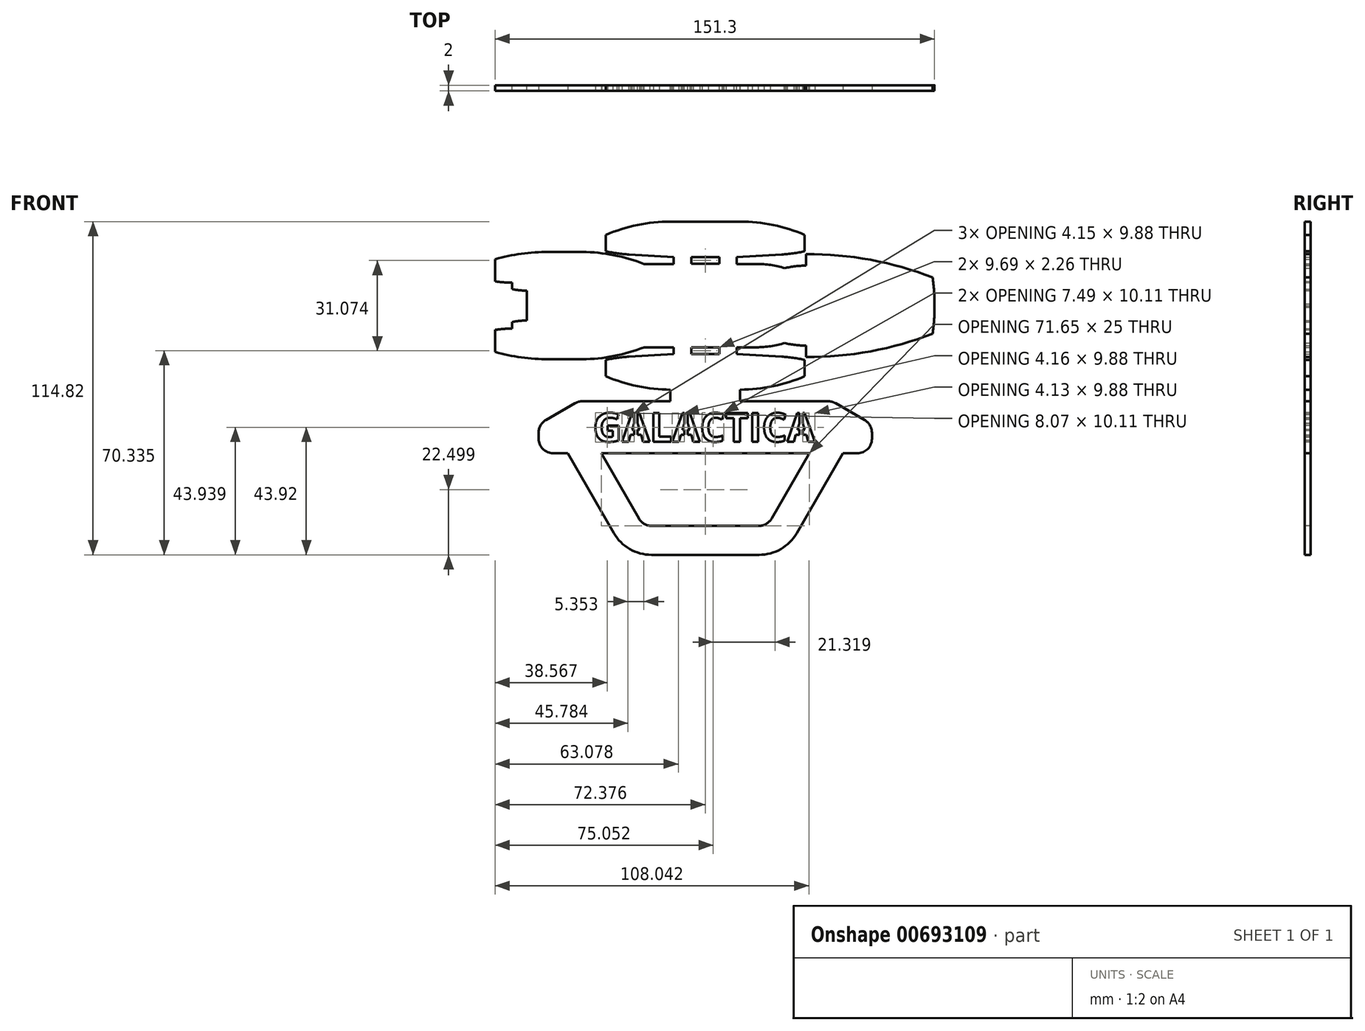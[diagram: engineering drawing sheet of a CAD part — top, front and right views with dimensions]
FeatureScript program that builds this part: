
annotation { "Feature Type Name" : "Feature", "Feature Type Description" : "" }
export const myFeature = defineFeature(function(context is Context, id is Id, definition is map)
    precondition{}
    {
        {
            var Q0;
            Q0=qCreatedBy(makeId("Front.planeOp"),FACE);
            var sketch = newSketch(context, id + "F0", { "sketchPlane" : qUnion([Q0])});
            skLineSegment(sketch, "E0", {"start": v(0, 27.3) * mm, "end": v(0, 0) * mm, "construction": true});
            skLineSegment(sketch, "E1", {"start": v(0, 0) * mm, "end": v(-65, 0) * mm, "construction": true});
            skArc(sketch, "E2", {"start": v(-25.69, 14.25) * mm, "mid": v(-44.18, 12.64) * mm, "end": v(-62.02, 7.56) * mm});
            skArc(sketch, "E3", {"start": v(-62.02, 7.56) * mm, "mid": v(-62.42, 3.79) * mm, "end": v(-62.55, 0) * mm});
            skLineSegment(sketch, "E4", {"start": v(-25.69, 14.25) * mm, "end": v(-25.69, 10.95) * mm});
            skArc(sketch, "E5", {"start": v(-19.6, 10.24) * mm, "mid": v(-22.62, 10.8) * mm, "end": v(-25.69, 10.95) * mm});
            skArc(sketch, "E6", {"start": v(-11.48, 11.46) * mm, "mid": v(-15.58, 11.15) * mm, "end": v(-19.6, 10.24) * mm});
            skLineSegment(sketch, "E7", {"start": v(-11.48, 11.46) * mm, "end": v(-5.84, 11.46) * mm});
            skLineSegment(sketch, "E8", {"start": v(-5.84, 11.46) * mm, "end": v(-5.84, 13.41) * mm});
            skLineSegment(sketch, "E9", {"start": v(-0.82, 11.5) * mm, "end": v(-0.82, 13.39) * mm});
            skLineSegment(sketch, "E10", {"start": v(-25.28, 19.79) * mm, "end": v(-25.28, 15.07) * mm});
            skArc(sketch, "E11", {"start": v(-25.28, 15.07) * mm, "mid": v(-22, 14.5) * mm, "end": v(-18.68, 14.17) * mm});
            skLineSegment(sketch, "E12", {"start": v(-18.68, 14.17) * mm, "end": v(-5.84, 13.41) * mm});
            skLineSegment(sketch, "E13", {"start": v(3.22, 14.5) * mm, "end": v(3.22, 0) * mm, "construction": true});
            skLineSegment(sketch, "E14.MirrorCS", {"start": v(7.26, 11.5) * mm, "end": v(7.26, 13.39) * mm});
            skLineSegment(sketch, "E15.MirrorCS", {"start": v(12.28, 11.46) * mm, "end": v(12.28, 13.41) * mm});
            skLineSegment(sketch, "E16.MirrorCS", {"start": v(31.72, 19.79) * mm, "end": v(31.72, 15.07) * mm});
            skLineSegment(sketch, "E17.MirrorCS", {"start": v(25.12, 14.17) * mm, "end": v(12.28, 13.41) * mm});
            skArc(sketch, "E18.MirrorCS", {"start": v(31.72, 15.07) * mm, "mid": v(28.44, 14.5) * mm, "end": v(25.12, 14.17) * mm});
            skArc(sketch, "E19", {"start": v(-6.78, 23.62) * mm, "mid": v(-16.23, 22.66) * mm, "end": v(-25.28, 19.79) * mm});
            skLineSegment(sketch, "E20", {"start": v(-6.78, 23.62) * mm, "end": v(13.22, 23.62) * mm});
            skArc(sketch, "E21.MirrorCS", {"start": v(13.22, 23.62) * mm, "mid": v(22.67, 22.66) * mm, "end": v(31.72, 19.79) * mm});
            skLineSegment(sketch, "E22", {"start": v(-0.82, 11.5) * mm, "end": v(7.26, 11.5) * mm});
            skLineSegment(sketch, "E23", {"start": v(-0.82, 13.39) * mm, "end": v(7.26, 13.39) * mm});
            skLineSegment(sketch, "E24", {"start": v(12.28, 11.46) * mm, "end": v(20.77, 11.46) * mm});
            skArc(sketch, "E25", {"start": v(38.48, 14.9) * mm, "mid": v(29.46, 14) * mm, "end": v(20.77, 11.46) * mm});
            skLineSegment(sketch, "E26", {"start": v(38.48, 14.9) * mm, "end": v(48.28, 14.9) * mm});
            skArc(sketch, "E27", {"start": v(63.53, 12.8) * mm, "mid": v(55.98, 14.37) * mm, "end": v(48.28, 14.9) * mm});
            skLineSegment(sketch, "E28", {"start": v(63.53, 12.8) * mm, "end": v(63.53, 6.47) * mm});
            skArc(sketch, "E29", {"start": v(58.7, 6.1) * mm, "mid": v(61.12, 6.19) * mm, "end": v(63.53, 6.47) * mm});
            skLineSegment(sketch, "E30", {"start": v(58.7, 6.1) * mm, "end": v(58.7, 4.24) * mm});
            skArc(sketch, "E31", {"start": v(54.38, 3.77) * mm, "mid": v(56.55, 3.9) * mm, "end": v(58.7, 4.24) * mm});
            skLineSegment(sketch, "E32", {"start": v(54.38, 3.77) * mm, "end": v(54.38, 0) * mm});
            skLineSegment(sketch, "E33", {"start": v(-62.55, 0) * mm, "end": v(-62.55, -0.5) * mm});
            skLineSegment(sketch, "E34", {"start": v(-62.55, -0.5) * mm, "end": v(54.38, -0.5) * mm, "construction": true});
            skLineSegment(sketch, "E35", {"start": v(54.38, -0.5) * mm, "end": v(54.38, 0) * mm});
            skArc(sketch, "E36.MirrorCS", {"start": v(58.7, -7.1) * mm, "mid": v(61.12, -7.19) * mm, "end": v(63.53, -7.47) * mm});
            skLineSegment(sketch, "E37.MirrorCS", {"start": v(-0.82, -12.5) * mm, "end": v(-0.82, -14.39) * mm});
            skLineSegment(sketch, "E38.MirrorCS", {"start": v(-25.28, -20.79) * mm, "end": v(-25.28, -16.07) * mm});
            skArc(sketch, "E39.MirrorCS", {"start": v(-25.28, -16.07) * mm, "mid": v(-22, -15.5) * mm, "end": v(-18.68, -15.17) * mm});
            skLineSegment(sketch, "E40.MirrorCS", {"start": v(58.7, -7.1) * mm, "end": v(58.7, -5.24) * mm});
            skLineSegment(sketch, "E41.MirrorCS", {"start": v(7.26, -12.5) * mm, "end": v(7.26, -14.39) * mm});
            skLineSegment(sketch, "E42.MirrorCS", {"start": v(54.38, -4.77) * mm, "end": v(54.38, -1) * mm});
            skLineSegment(sketch, "E43.MirrorCS", {"start": v(12.28, -12.46) * mm, "end": v(12.28, -14.41) * mm});
            skLineSegment(sketch, "E44.MirrorCS", {"start": v(-62.55, -1) * mm, "end": v(-62.55, -0.5) * mm});
            skArc(sketch, "E45.MirrorCS", {"start": v(54.38, -4.77) * mm, "mid": v(56.55, -4.9) * mm, "end": v(58.7, -5.24) * mm});
            skLineSegment(sketch, "E46.MirrorCS", {"start": v(-25.69, -15.25) * mm, "end": v(-25.69, -11.95) * mm});
            skLineSegment(sketch, "E47.MirrorCS", {"start": v(31.72, -20.79) * mm, "end": v(31.72, -16.07) * mm});
            skLineSegment(sketch, "E48.MirrorCS", {"start": v(54.38, -0.5) * mm, "end": v(54.38, -1) * mm});
            skLineSegment(sketch, "E49.MirrorCS", {"start": v(-5.84, -12.46) * mm, "end": v(-5.84, -14.41) * mm});
            skLineSegment(sketch, "E50.MirrorCS", {"start": v(-11.48, -12.46) * mm, "end": v(-5.84, -12.46) * mm});
            skArc(sketch, "E51.MirrorCS", {"start": v(-19.6, -11.24) * mm, "mid": v(-22.62, -11.8) * mm, "end": v(-25.69, -11.95) * mm});
            skLineSegment(sketch, "E52.MirrorCS", {"start": v(-0.82, -12.5) * mm, "end": v(7.26, -12.5) * mm});
            skLineSegment(sketch, "E53.MirrorCS", {"start": v(-0.82, -14.39) * mm, "end": v(7.26, -14.39) * mm});
            skArc(sketch, "E54.MirrorCS", {"start": v(13.22, -24.62) * mm, "mid": v(22.67, -23.66) * mm, "end": v(31.72, -20.79) * mm});
            skArc(sketch, "E55.MirrorCS", {"start": v(31.72, -16.07) * mm, "mid": v(28.44, -15.5) * mm, "end": v(25.12, -15.17) * mm});
            skLineSegment(sketch, "E56.MirrorCS", {"start": v(0, -28.3) * mm, "end": v(0, -1) * mm, "construction": true});
            skLineSegment(sketch, "E57.MirrorCS", {"start": v(63.53, -13.8) * mm, "end": v(63.53, -7.47) * mm});
            skArc(sketch, "E58.MirrorCS", {"start": v(38.48, -15.9) * mm, "mid": v(29.46, -15) * mm, "end": v(20.77, -12.46) * mm});
            skLineSegment(sketch, "E59.MirrorCS", {"start": v(-18.68, -15.17) * mm, "end": v(-5.84, -14.41) * mm});
            skLineSegment(sketch, "E60.MirrorCS", {"start": v(25.12, -15.17) * mm, "end": v(12.28, -14.41) * mm});
            skLineSegment(sketch, "E61.MirrorCS", {"start": v(38.48, -15.9) * mm, "end": v(48.28, -15.9) * mm});
            skLineSegment(sketch, "E62.MirrorCS", {"start": v(3.22, -15.5) * mm, "end": v(3.22, -1) * mm, "construction": true});
            skLineSegment(sketch, "E63.MirrorCS", {"start": v(0, -1) * mm, "end": v(-65, -1) * mm, "construction": true});
            skLineSegment(sketch, "E64.MirrorCS", {"start": v(12.28, -12.46) * mm, "end": v(20.77, -12.46) * mm});
            skArc(sketch, "E65.MirrorCS", {"start": v(63.53, -13.8) * mm, "mid": v(55.98, -15.37) * mm, "end": v(48.28, -15.9) * mm});
            skArc(sketch, "E66.MirrorCS", {"start": v(-25.69, -15.25) * mm, "mid": v(-44.18, -13.64) * mm, "end": v(-62.02, -8.56) * mm});
            skArc(sketch, "E67.MirrorCS", {"start": v(-62.02, -8.56) * mm, "mid": v(-62.42, -4.79) * mm, "end": v(-62.55, -1) * mm});
            skLineSegment(sketch, "E68.MirrorCS", {"start": v(-6.78, -24.62) * mm, "end": v(13.22, -24.62) * mm});
            skArc(sketch, "E69.MirrorCS", {"start": v(-6.78, -24.62) * mm, "mid": v(-16.23, -23.66) * mm, "end": v(-25.28, -20.79) * mm});
            skArc(sketch, "E70.MirrorCS", {"start": v(-11.48, -12.46) * mm, "mid": v(-15.58, -12.15) * mm, "end": v(-19.6, -11.24) * mm});
            skSolve(sketch);
        }
        {
            var Q0;
            Q0=makeQuery(id+"F0.imprint","IMPRINT",FACE,{"disambiguationData":[TD([[makeQuery(id+"F0.imprint","IMPRINT",EDGE,{"derivedFrom":sQuery(id+"F0.wireOp",EDGE,"E2")}),1.0]])]});
            extrude(context, id + "F1", {"entities" : qUnion([Q0]), "depth" : 2 * mm, "offsetDistance" : 25 * mm});
        }
        {
            var Q0;
            Q0=makeQuery(id+"F1.opExtrude","SWEPT_BODY",BODY,{"disambiguationData":[OSD([sQuery(id+"F0.wireOp",EDGE,"E2"),sQuery(id+"F0.wireOp",EDGE,"E3"),sQuery(id+"F0.wireOp",EDGE,"E4"),sQuery(id+"F0.wireOp",EDGE,"E5"),sQuery(id+"F0.wireOp",EDGE,"E6"),sQuery(id+"F0.wireOp",EDGE,"E7"),sQuery(id+"F0.wireOp",EDGE,"E8"),sQuery(id+"F0.wireOp",EDGE,"E9"),sQuery(id+"F0.wireOp",EDGE,"E10"),sQuery(id+"F0.wireOp",EDGE,"E11"),sQuery(id+"F0.wireOp",EDGE,"E12"),sQuery(id+"F0.wireOp",EDGE,"E14.MirrorCS"),sQuery(id+"F0.wireOp",EDGE,"E15.MirrorCS"),sQuery(id+"F0.wireOp",EDGE,"E16.MirrorCS"),sQuery(id+"F0.wireOp",EDGE,"E17.MirrorCS"),sQuery(id+"F0.wireOp",EDGE,"E18.MirrorCS"),sQuery(id+"F0.wireOp",EDGE,"E19"),sQuery(id+"F0.wireOp",EDGE,"E20"),sQuery(id+"F0.wireOp",EDGE,"E21.MirrorCS"),sQuery(id+"F0.wireOp",EDGE,"E22"),sQuery(id+"F0.wireOp",EDGE,"E23"),sQuery(id+"F0.wireOp",EDGE,"E24"),sQuery(id+"F0.wireOp",EDGE,"E25"),sQuery(id+"F0.wireOp",EDGE,"E26"),sQuery(id+"F0.wireOp",EDGE,"E27"),sQuery(id+"F0.wireOp",EDGE,"E28"),sQuery(id+"F0.wireOp",EDGE,"E29"),sQuery(id+"F0.wireOp",EDGE,"E30"),sQuery(id+"F0.wireOp",EDGE,"E31"),sQuery(id+"F0.wireOp",EDGE,"E32"),sQuery(id+"F0.wireOp",EDGE,"E33"),sQuery(id+"F0.wireOp",EDGE,"E35"),sQuery(id+"F0.wireOp",EDGE,"E36.MirrorCS"),sQuery(id+"F0.wireOp",EDGE,"E37.MirrorCS"),sQuery(id+"F0.wireOp",EDGE,"E38.MirrorCS"),sQuery(id+"F0.wireOp",EDGE,"E39.MirrorCS"),sQuery(id+"F0.wireOp",EDGE,"E40.MirrorCS"),sQuery(id+"F0.wireOp",EDGE,"E41.MirrorCS"),sQuery(id+"F0.wireOp",EDGE,"E42.MirrorCS"),sQuery(id+"F0.wireOp",EDGE,"E43.MirrorCS"),sQuery(id+"F0.wireOp",EDGE,"E44.MirrorCS"),sQuery(id+"F0.wireOp",EDGE,"E45.MirrorCS"),sQuery(id+"F0.wireOp",EDGE,"E46.MirrorCS"),sQuery(id+"F0.wireOp",EDGE,"E47.MirrorCS"),sQuery(id+"F0.wireOp",EDGE,"E48.MirrorCS"),sQuery(id+"F0.wireOp",EDGE,"E49.MirrorCS"),sQuery(id+"F0.wireOp",EDGE,"E50.MirrorCS"),sQuery(id+"F0.wireOp",EDGE,"E51.MirrorCS"),sQuery(id+"F0.wireOp",EDGE,"E52.MirrorCS"),sQuery(id+"F0.wireOp",EDGE,"E53.MirrorCS"),sQuery(id+"F0.wireOp",EDGE,"E54.MirrorCS"),sQuery(id+"F0.wireOp",EDGE,"E55.MirrorCS"),sQuery(id+"F0.wireOp",EDGE,"E57.MirrorCS"),sQuery(id+"F0.wireOp",EDGE,"E58.MirrorCS"),sQuery(id+"F0.wireOp",EDGE,"E59.MirrorCS"),sQuery(id+"F0.wireOp",EDGE,"E60.MirrorCS"),sQuery(id+"F0.wireOp",EDGE,"E61.MirrorCS"),sQuery(id+"F0.wireOp",EDGE,"E64.MirrorCS"),sQuery(id+"F0.wireOp",EDGE,"E65.MirrorCS"),sQuery(id+"F0.wireOp",EDGE,"E66.MirrorCS"),sQuery(id+"F0.wireOp",EDGE,"E67.MirrorCS"),sQuery(id+"F0.wireOp",EDGE,"E68.MirrorCS"),sQuery(id+"F0.wireOp",EDGE,"E69.MirrorCS"),sQuery(id+"F0.wireOp",EDGE,"E70.MirrorCS")])]});
            var Q1;
            Q1=makeQuery(id+"F1.opExtrude","SWEPT_EDGE",EDGE,{"disambiguationData":[OSD([sQuery(id+"F0.wireOp",EDGE,"E9"),sQuery(id+"F0.wireOp",EDGE,"E22")])]});
            transform(context, id + "F2", {"entities" : qUnion([Q0]), "transformType" : TransformType.ROTATION, "transformAxis" : qUnion([Q1]), "angle" : 180 * degree, "makeCopy" : false});
        }
        {
            var Q0;
            Q0=makeQuery(id+"F1.opExtrude","SWEPT_BODY",BODY,{"disambiguationData":[OSD([sQuery(id+"F0.wireOp",EDGE,"E2"),sQuery(id+"F0.wireOp",EDGE,"E3"),sQuery(id+"F0.wireOp",EDGE,"E4"),sQuery(id+"F0.wireOp",EDGE,"E5"),sQuery(id+"F0.wireOp",EDGE,"E6"),sQuery(id+"F0.wireOp",EDGE,"E7"),sQuery(id+"F0.wireOp",EDGE,"E8"),sQuery(id+"F0.wireOp",EDGE,"E9"),sQuery(id+"F0.wireOp",EDGE,"E10"),sQuery(id+"F0.wireOp",EDGE,"E11"),sQuery(id+"F0.wireOp",EDGE,"E12"),sQuery(id+"F0.wireOp",EDGE,"E14.MirrorCS"),sQuery(id+"F0.wireOp",EDGE,"E15.MirrorCS"),sQuery(id+"F0.wireOp",EDGE,"E16.MirrorCS"),sQuery(id+"F0.wireOp",EDGE,"E17.MirrorCS"),sQuery(id+"F0.wireOp",EDGE,"E18.MirrorCS"),sQuery(id+"F0.wireOp",EDGE,"E19"),sQuery(id+"F0.wireOp",EDGE,"E20"),sQuery(id+"F0.wireOp",EDGE,"E21.MirrorCS"),sQuery(id+"F0.wireOp",EDGE,"E22"),sQuery(id+"F0.wireOp",EDGE,"E23"),sQuery(id+"F0.wireOp",EDGE,"E24"),sQuery(id+"F0.wireOp",EDGE,"E25"),sQuery(id+"F0.wireOp",EDGE,"E26"),sQuery(id+"F0.wireOp",EDGE,"E27"),sQuery(id+"F0.wireOp",EDGE,"E28"),sQuery(id+"F0.wireOp",EDGE,"E29"),sQuery(id+"F0.wireOp",EDGE,"E30"),sQuery(id+"F0.wireOp",EDGE,"E31"),sQuery(id+"F0.wireOp",EDGE,"E32"),sQuery(id+"F0.wireOp",EDGE,"E33"),sQuery(id+"F0.wireOp",EDGE,"E35"),sQuery(id+"F0.wireOp",EDGE,"E36.MirrorCS"),sQuery(id+"F0.wireOp",EDGE,"E37.MirrorCS"),sQuery(id+"F0.wireOp",EDGE,"E38.MirrorCS"),sQuery(id+"F0.wireOp",EDGE,"E39.MirrorCS"),sQuery(id+"F0.wireOp",EDGE,"E40.MirrorCS"),sQuery(id+"F0.wireOp",EDGE,"E41.MirrorCS"),sQuery(id+"F0.wireOp",EDGE,"E42.MirrorCS"),sQuery(id+"F0.wireOp",EDGE,"E43.MirrorCS"),sQuery(id+"F0.wireOp",EDGE,"E44.MirrorCS"),sQuery(id+"F0.wireOp",EDGE,"E45.MirrorCS"),sQuery(id+"F0.wireOp",EDGE,"E46.MirrorCS"),sQuery(id+"F0.wireOp",EDGE,"E47.MirrorCS"),sQuery(id+"F0.wireOp",EDGE,"E48.MirrorCS"),sQuery(id+"F0.wireOp",EDGE,"E49.MirrorCS"),sQuery(id+"F0.wireOp",EDGE,"E50.MirrorCS"),sQuery(id+"F0.wireOp",EDGE,"E51.MirrorCS"),sQuery(id+"F0.wireOp",EDGE,"E52.MirrorCS"),sQuery(id+"F0.wireOp",EDGE,"E53.MirrorCS"),sQuery(id+"F0.wireOp",EDGE,"E54.MirrorCS"),sQuery(id+"F0.wireOp",EDGE,"E55.MirrorCS"),sQuery(id+"F0.wireOp",EDGE,"E57.MirrorCS"),sQuery(id+"F0.wireOp",EDGE,"E58.MirrorCS"),sQuery(id+"F0.wireOp",EDGE,"E59.MirrorCS"),sQuery(id+"F0.wireOp",EDGE,"E60.MirrorCS"),sQuery(id+"F0.wireOp",EDGE,"E61.MirrorCS"),sQuery(id+"F0.wireOp",EDGE,"E64.MirrorCS"),sQuery(id+"F0.wireOp",EDGE,"E65.MirrorCS"),sQuery(id+"F0.wireOp",EDGE,"E66.MirrorCS"),sQuery(id+"F0.wireOp",EDGE,"E67.MirrorCS"),sQuery(id+"F0.wireOp",EDGE,"E68.MirrorCS"),sQuery(id+"F0.wireOp",EDGE,"E69.MirrorCS"),sQuery(id+"F0.wireOp",EDGE,"E70.MirrorCS")])]});
            var Q1;
            Q1=makeQuery(id+"F1.opExtrude","CAP_VERTEX",VERTEX,{"disambiguationData":[OSD([sQuery(id+"F0.wireOp",EDGE,"E27"),sQuery(id+"F0.wireOp",EDGE,"E28")])],"isStart":false});
            transform(context, id + "F3", {"entities" : qUnion([Q0]), "transformType" : TransformType.SCALE_UNIFORMLY, "scale" : 1.2, "scalePoint" : qUnion([Q1]), "makeCopy" : false});
        }
        {
            var Q0;
            Q0=makeQuery(id+"F1.opExtrude","CAP_FACE",FACE,{"disambiguationData":[OSD([sQuery(id+"F0.wireOp",EDGE,"E2"),sQuery(id+"F0.wireOp",EDGE,"E3"),sQuery(id+"F0.wireOp",EDGE,"E4"),sQuery(id+"F0.wireOp",EDGE,"E5"),sQuery(id+"F0.wireOp",EDGE,"E6"),sQuery(id+"F0.wireOp",EDGE,"E7"),sQuery(id+"F0.wireOp",EDGE,"E8"),sQuery(id+"F0.wireOp",EDGE,"E9"),sQuery(id+"F0.wireOp",EDGE,"E10"),sQuery(id+"F0.wireOp",EDGE,"E11"),sQuery(id+"F0.wireOp",EDGE,"E12"),sQuery(id+"F0.wireOp",EDGE,"E14.MirrorCS"),sQuery(id+"F0.wireOp",EDGE,"E15.MirrorCS"),sQuery(id+"F0.wireOp",EDGE,"E16.MirrorCS"),sQuery(id+"F0.wireOp",EDGE,"E17.MirrorCS"),sQuery(id+"F0.wireOp",EDGE,"E18.MirrorCS"),sQuery(id+"F0.wireOp",EDGE,"E19"),sQuery(id+"F0.wireOp",EDGE,"E20"),sQuery(id+"F0.wireOp",EDGE,"E21.MirrorCS"),sQuery(id+"F0.wireOp",EDGE,"E22"),sQuery(id+"F0.wireOp",EDGE,"E23"),sQuery(id+"F0.wireOp",EDGE,"E24"),sQuery(id+"F0.wireOp",EDGE,"E25"),sQuery(id+"F0.wireOp",EDGE,"E26"),sQuery(id+"F0.wireOp",EDGE,"E27"),sQuery(id+"F0.wireOp",EDGE,"E28"),sQuery(id+"F0.wireOp",EDGE,"E29"),sQuery(id+"F0.wireOp",EDGE,"E30"),sQuery(id+"F0.wireOp",EDGE,"E31"),sQuery(id+"F0.wireOp",EDGE,"E32"),sQuery(id+"F0.wireOp",EDGE,"E33"),sQuery(id+"F0.wireOp",EDGE,"E35"),sQuery(id+"F0.wireOp",EDGE,"E36.MirrorCS"),sQuery(id+"F0.wireOp",EDGE,"E37.MirrorCS"),sQuery(id+"F0.wireOp",EDGE,"E38.MirrorCS"),sQuery(id+"F0.wireOp",EDGE,"E39.MirrorCS"),sQuery(id+"F0.wireOp",EDGE,"E40.MirrorCS"),sQuery(id+"F0.wireOp",EDGE,"E41.MirrorCS"),sQuery(id+"F0.wireOp",EDGE,"E42.MirrorCS"),sQuery(id+"F0.wireOp",EDGE,"E43.MirrorCS"),sQuery(id+"F0.wireOp",EDGE,"E44.MirrorCS"),sQuery(id+"F0.wireOp",EDGE,"E45.MirrorCS"),sQuery(id+"F0.wireOp",EDGE,"E46.MirrorCS"),sQuery(id+"F0.wireOp",EDGE,"E47.MirrorCS"),sQuery(id+"F0.wireOp",EDGE,"E48.MirrorCS"),sQuery(id+"F0.wireOp",EDGE,"E49.MirrorCS"),sQuery(id+"F0.wireOp",EDGE,"E50.MirrorCS"),sQuery(id+"F0.wireOp",EDGE,"E51.MirrorCS"),sQuery(id+"F0.wireOp",EDGE,"E52.MirrorCS"),sQuery(id+"F0.wireOp",EDGE,"E53.MirrorCS"),sQuery(id+"F0.wireOp",EDGE,"E54.MirrorCS"),sQuery(id+"F0.wireOp",EDGE,"E55.MirrorCS"),sQuery(id+"F0.wireOp",EDGE,"E57.MirrorCS"),sQuery(id+"F0.wireOp",EDGE,"E58.MirrorCS"),sQuery(id+"F0.wireOp",EDGE,"E59.MirrorCS"),sQuery(id+"F0.wireOp",EDGE,"E60.MirrorCS"),sQuery(id+"F0.wireOp",EDGE,"E61.MirrorCS"),sQuery(id+"F0.wireOp",EDGE,"E64.MirrorCS"),sQuery(id+"F0.wireOp",EDGE,"E65.MirrorCS"),sQuery(id+"F0.wireOp",EDGE,"E66.MirrorCS"),sQuery(id+"F0.wireOp",EDGE,"E67.MirrorCS"),sQuery(id+"F0.wireOp",EDGE,"E68.MirrorCS"),sQuery(id+"F0.wireOp",EDGE,"E69.MirrorCS"),sQuery(id+"F0.wireOp",EDGE,"E70.MirrorCS")])],"isStart":false});
            var sketch = newSketch(context, id + "F4", { "sketchPlane" : qUnion([Q0])});
            skLineSegment(sketch, "E71", {"start": v(-4.8, -2.78) * mm, "end": v(-4.8, -6.78) * mm});
            skLineSegment(sketch, "E72", {"start": v(19.2, -2.78) * mm, "end": v(19.2, -6.78) * mm});
            skLineSegment(sketch, "E73", {"start": v(-4.8, -6.78) * mm, "end": v(-36.44, -6.78) * mm});
            skLineSegment(sketch, "E74", {"start": v(-36.44, -6.78) * mm, "end": v(-50.17, -14.7) * mm});
            skLineSegment(sketch, "E75", {"start": v(-50.17, -14.7) * mm, "end": v(-50.17, -24.7) * mm});
            skLineSegment(sketch, "E76", {"start": v(-50.17, -24.7) * mm, "end": v(64.58, -24.7) * mm});
            skLineSegment(sketch, "E77", {"start": v(64.58, -24.7) * mm, "end": v(64.58, -14.7) * mm});
            skLineSegment(sketch, "E78", {"start": v(64.58, -14.7) * mm, "end": v(50.85, -6.78) * mm});
            skLineSegment(sketch, "E79", {"start": v(50.85, -6.78) * mm, "end": v(19.2, -6.78) * mm});
            skLineSegment(sketch, "E80", {"start": v(-4.8, -2.78) * mm, "end": v(19.2, -2.78) * mm});
            skLineSegment(sketch, "E81", {"start": v(7.2, -2.78) * mm, "end": v(7.2, -24.7) * mm, "construction": true});
            skPoint(sketch, "E81.endSnap0", {"position": v(7.2, -24.7) * mm});
            skText(sketch, "E82", { "text": "GALACTICA", "fontName": "OpenSans-Bold.ttf"});
            const initialGuessF4  = {"E82": [-0.03144, -0.0207, 1, 0, 0.00992]};
            skSetInitialGuess(sketch, initialGuessF4);
            skSolve(sketch);
        }
        {
            var Q0;
            Q0 = qSketchRegion(id + "F4", true);
            var Q1;
            Q1=makeQuery(id+"F4.imprint","IMPRINT",FACE,{"disambiguationData":[TD([[makeQuery(id+"F4.imprint","IMPRINT",EDGE,{"derivedFrom":sQuery(id+"F4.wireOp",EDGE,"E82.sketch_text.stroke-27")}),1.0]])]});
            var Q2;
            Q2=makeQuery(id+"F4.imprint","IMPRINT",FACE,{"disambiguationData":[TD([[makeQuery(id+"F4.imprint","IMPRINT",EDGE,{"derivedFrom":sQuery(id+"F4.wireOp",EDGE,"E82.sketch_text.stroke-45")}),1.0]])]});
            var Q3;
            Q3=makeQuery(id+"F4.imprint","IMPRINT",FACE,{"disambiguationData":[TD([[makeQuery(id+"F4.imprint","IMPRINT",EDGE,{"derivedFrom":sQuery(id+"F4.wireOp",EDGE,"E82.sketch_text.stroke-99")}),1.0]])]});
            var Q4;
            Q4=makeQuery(id+"F1.opExtrude","CAP_FACE",FACE,{"disambiguationData":[OSD([sQuery(id+"F0.wireOp",EDGE,"E2"),sQuery(id+"F0.wireOp",EDGE,"E3"),sQuery(id+"F0.wireOp",EDGE,"E4"),sQuery(id+"F0.wireOp",EDGE,"E5"),sQuery(id+"F0.wireOp",EDGE,"E6"),sQuery(id+"F0.wireOp",EDGE,"E7"),sQuery(id+"F0.wireOp",EDGE,"E8"),sQuery(id+"F0.wireOp",EDGE,"E9"),sQuery(id+"F0.wireOp",EDGE,"E10"),sQuery(id+"F0.wireOp",EDGE,"E11"),sQuery(id+"F0.wireOp",EDGE,"E12"),sQuery(id+"F0.wireOp",EDGE,"E14.MirrorCS"),sQuery(id+"F0.wireOp",EDGE,"E15.MirrorCS"),sQuery(id+"F0.wireOp",EDGE,"E16.MirrorCS"),sQuery(id+"F0.wireOp",EDGE,"E17.MirrorCS"),sQuery(id+"F0.wireOp",EDGE,"E18.MirrorCS"),sQuery(id+"F0.wireOp",EDGE,"E19"),sQuery(id+"F0.wireOp",EDGE,"E20"),sQuery(id+"F0.wireOp",EDGE,"E21.MirrorCS"),sQuery(id+"F0.wireOp",EDGE,"E22"),sQuery(id+"F0.wireOp",EDGE,"E23"),sQuery(id+"F0.wireOp",EDGE,"E24"),sQuery(id+"F0.wireOp",EDGE,"E25"),sQuery(id+"F0.wireOp",EDGE,"E26"),sQuery(id+"F0.wireOp",EDGE,"E27"),sQuery(id+"F0.wireOp",EDGE,"E28"),sQuery(id+"F0.wireOp",EDGE,"E29"),sQuery(id+"F0.wireOp",EDGE,"E30"),sQuery(id+"F0.wireOp",EDGE,"E31"),sQuery(id+"F0.wireOp",EDGE,"E32"),sQuery(id+"F0.wireOp",EDGE,"E33"),sQuery(id+"F0.wireOp",EDGE,"E35"),sQuery(id+"F0.wireOp",EDGE,"E36.MirrorCS"),sQuery(id+"F0.wireOp",EDGE,"E37.MirrorCS"),sQuery(id+"F0.wireOp",EDGE,"E38.MirrorCS"),sQuery(id+"F0.wireOp",EDGE,"E39.MirrorCS"),sQuery(id+"F0.wireOp",EDGE,"E40.MirrorCS"),sQuery(id+"F0.wireOp",EDGE,"E41.MirrorCS"),sQuery(id+"F0.wireOp",EDGE,"E42.MirrorCS"),sQuery(id+"F0.wireOp",EDGE,"E43.MirrorCS"),sQuery(id+"F0.wireOp",EDGE,"E44.MirrorCS"),sQuery(id+"F0.wireOp",EDGE,"E45.MirrorCS"),sQuery(id+"F0.wireOp",EDGE,"E46.MirrorCS"),sQuery(id+"F0.wireOp",EDGE,"E47.MirrorCS"),sQuery(id+"F0.wireOp",EDGE,"E48.MirrorCS"),sQuery(id+"F0.wireOp",EDGE,"E49.MirrorCS"),sQuery(id+"F0.wireOp",EDGE,"E50.MirrorCS"),sQuery(id+"F0.wireOp",EDGE,"E51.MirrorCS"),sQuery(id+"F0.wireOp",EDGE,"E52.MirrorCS"),sQuery(id+"F0.wireOp",EDGE,"E53.MirrorCS"),sQuery(id+"F0.wireOp",EDGE,"E54.MirrorCS"),sQuery(id+"F0.wireOp",EDGE,"E55.MirrorCS"),sQuery(id+"F0.wireOp",EDGE,"E57.MirrorCS"),sQuery(id+"F0.wireOp",EDGE,"E58.MirrorCS"),sQuery(id+"F0.wireOp",EDGE,"E59.MirrorCS"),sQuery(id+"F0.wireOp",EDGE,"E60.MirrorCS"),sQuery(id+"F0.wireOp",EDGE,"E61.MirrorCS"),sQuery(id+"F0.wireOp",EDGE,"E64.MirrorCS"),sQuery(id+"F0.wireOp",EDGE,"E65.MirrorCS"),sQuery(id+"F0.wireOp",EDGE,"E66.MirrorCS"),sQuery(id+"F0.wireOp",EDGE,"E67.MirrorCS"),sQuery(id+"F0.wireOp",EDGE,"E68.MirrorCS"),sQuery(id+"F0.wireOp",EDGE,"E69.MirrorCS"),sQuery(id+"F0.wireOp",EDGE,"E70.MirrorCS")])],"isStart":true});
            extrude(context, id + "F5", {"entities" : qUnion([Q0, Q1, Q2, Q3]), "operationType" : NewBodyOperationType.ADD, "endBound" : BoundingType.UP_TO_SURFACE, "oppositeDirection" : true, "depth" : 25 * mm, "endBoundEntityFace" : qUnion([Q4]), "offsetDistance" : 25 * mm});
        }
        {
            var Q0;
            Q0=makeQuery(id+"F5.boolean.opBoolean","MERGE",FACE,{"derivedFrom":[makeQuery(id+"F1.opExtrude","CAP_FACE",FACE,{"disambiguationData":[OSD([sQuery(id+"F0.wireOp",EDGE,"E2"),sQuery(id+"F0.wireOp",EDGE,"E3"),sQuery(id+"F0.wireOp",EDGE,"E4"),sQuery(id+"F0.wireOp",EDGE,"E5"),sQuery(id+"F0.wireOp",EDGE,"E6"),sQuery(id+"F0.wireOp",EDGE,"E7"),sQuery(id+"F0.wireOp",EDGE,"E8"),sQuery(id+"F0.wireOp",EDGE,"E9"),sQuery(id+"F0.wireOp",EDGE,"E10"),sQuery(id+"F0.wireOp",EDGE,"E11"),sQuery(id+"F0.wireOp",EDGE,"E12"),sQuery(id+"F0.wireOp",EDGE,"E14.MirrorCS"),sQuery(id+"F0.wireOp",EDGE,"E15.MirrorCS"),sQuery(id+"F0.wireOp",EDGE,"E16.MirrorCS"),sQuery(id+"F0.wireOp",EDGE,"E17.MirrorCS"),sQuery(id+"F0.wireOp",EDGE,"E18.MirrorCS"),sQuery(id+"F0.wireOp",EDGE,"E19"),sQuery(id+"F0.wireOp",EDGE,"E20"),sQuery(id+"F0.wireOp",EDGE,"E21.MirrorCS"),sQuery(id+"F0.wireOp",EDGE,"E22"),sQuery(id+"F0.wireOp",EDGE,"E23"),sQuery(id+"F0.wireOp",EDGE,"E24"),sQuery(id+"F0.wireOp",EDGE,"E25"),sQuery(id+"F0.wireOp",EDGE,"E26"),sQuery(id+"F0.wireOp",EDGE,"E27"),sQuery(id+"F0.wireOp",EDGE,"E28"),sQuery(id+"F0.wireOp",EDGE,"E29"),sQuery(id+"F0.wireOp",EDGE,"E30"),sQuery(id+"F0.wireOp",EDGE,"E31"),sQuery(id+"F0.wireOp",EDGE,"E32"),sQuery(id+"F0.wireOp",EDGE,"E33"),sQuery(id+"F0.wireOp",EDGE,"E35"),sQuery(id+"F0.wireOp",EDGE,"E36.MirrorCS"),sQuery(id+"F0.wireOp",EDGE,"E37.MirrorCS"),sQuery(id+"F0.wireOp",EDGE,"E38.MirrorCS"),sQuery(id+"F0.wireOp",EDGE,"E39.MirrorCS"),sQuery(id+"F0.wireOp",EDGE,"E40.MirrorCS"),sQuery(id+"F0.wireOp",EDGE,"E41.MirrorCS"),sQuery(id+"F0.wireOp",EDGE,"E42.MirrorCS"),sQuery(id+"F0.wireOp",EDGE,"E43.MirrorCS"),sQuery(id+"F0.wireOp",EDGE,"E44.MirrorCS"),sQuery(id+"F0.wireOp",EDGE,"E45.MirrorCS"),sQuery(id+"F0.wireOp",EDGE,"E46.MirrorCS"),sQuery(id+"F0.wireOp",EDGE,"E47.MirrorCS"),sQuery(id+"F0.wireOp",EDGE,"E48.MirrorCS"),sQuery(id+"F0.wireOp",EDGE,"E49.MirrorCS"),sQuery(id+"F0.wireOp",EDGE,"E50.MirrorCS"),sQuery(id+"F0.wireOp",EDGE,"E51.MirrorCS"),sQuery(id+"F0.wireOp",EDGE,"E52.MirrorCS"),sQuery(id+"F0.wireOp",EDGE,"E53.MirrorCS"),sQuery(id+"F0.wireOp",EDGE,"E54.MirrorCS"),sQuery(id+"F0.wireOp",EDGE,"E55.MirrorCS"),sQuery(id+"F0.wireOp",EDGE,"E57.MirrorCS"),sQuery(id+"F0.wireOp",EDGE,"E58.MirrorCS"),sQuery(id+"F0.wireOp",EDGE,"E59.MirrorCS"),sQuery(id+"F0.wireOp",EDGE,"E60.MirrorCS"),sQuery(id+"F0.wireOp",EDGE,"E61.MirrorCS"),sQuery(id+"F0.wireOp",EDGE,"E64.MirrorCS"),sQuery(id+"F0.wireOp",EDGE,"E65.MirrorCS"),sQuery(id+"F0.wireOp",EDGE,"E66.MirrorCS"),sQuery(id+"F0.wireOp",EDGE,"E67.MirrorCS"),sQuery(id+"F0.wireOp",EDGE,"E68.MirrorCS"),sQuery(id+"F0.wireOp",EDGE,"E69.MirrorCS"),sQuery(id+"F0.wireOp",EDGE,"E70.MirrorCS")])],"isStart":false}),makeQuery(id+"F5.opExtrude","CAP_FACE",FACE,{"disambiguationData":[OSD([sQuery(id+"F4.wireOp",EDGE,"E71"),sQuery(id+"F4.wireOp",EDGE,"E72"),sQuery(id+"F4.wireOp",EDGE,"E73"),sQuery(id+"F4.wireOp",EDGE,"E74"),sQuery(id+"F4.wireOp",EDGE,"E75"),sQuery(id+"F4.wireOp",EDGE,"E76"),sQuery(id+"F4.wireOp",EDGE,"E77"),sQuery(id+"F4.wireOp",EDGE,"E78"),sQuery(id+"F4.wireOp",EDGE,"E79"),sQuery(id+"F4.wireOp",EDGE,"E80"),sQuery(id+"F4.wireOp",EDGE,"E82.sketch_text.stroke-0"),sQuery(id+"F4.wireOp",EDGE,"E82.sketch_text.stroke-1"),sQuery(id+"F4.wireOp",EDGE,"E82.sketch_text.stroke-2"),sQuery(id+"F4.wireOp",EDGE,"E82.sketch_text.stroke-3"),sQuery(id+"F4.wireOp",EDGE,"E82.sketch_text.stroke-4"),sQuery(id+"F4.wireOp",EDGE,"E82.sketch_text.stroke-5"),sQuery(id+"F4.wireOp",EDGE,"E82.sketch_text.stroke-6"),sQuery(id+"F4.wireOp",EDGE,"E82.sketch_text.stroke-7"),sQuery(id+"F4.wireOp",EDGE,"E82.sketch_text.stroke-8"),sQuery(id+"F4.wireOp",EDGE,"E82.sketch_text.stroke-9"),sQuery(id+"F4.wireOp",EDGE,"E82.sketch_text.stroke-10"),sQuery(id+"F4.wireOp",EDGE,"E82.sketch_text.stroke-11"),sQuery(id+"F4.wireOp",EDGE,"E82.sketch_text.stroke-12"),sQuery(id+"F4.wireOp",EDGE,"E82.sketch_text.stroke-13"),sQuery(id+"F4.wireOp",EDGE,"E82.sketch_text.stroke-14"),sQuery(id+"F4.wireOp",EDGE,"E82.sketch_text.stroke-15"),sQuery(id+"F4.wireOp",EDGE,"E82.sketch_text.stroke-16"),sQuery(id+"F4.wireOp",EDGE,"E82.sketch_text.stroke-17"),sQuery(id+"F4.wireOp",EDGE,"E82.sketch_text.stroke-18"),sQuery(id+"F4.wireOp",EDGE,"E82.sketch_text.stroke-19"),sQuery(id+"F4.wireOp",EDGE,"E82.sketch_text.stroke-20"),sQuery(id+"F4.wireOp",EDGE,"E82.sketch_text.stroke-21"),sQuery(id+"F4.wireOp",EDGE,"E82.sketch_text.stroke-22"),sQuery(id+"F4.wireOp",EDGE,"E82.sketch_text.stroke-23"),sQuery(id+"F4.wireOp",EDGE,"E82.sketch_text.stroke-24"),sQuery(id+"F4.wireOp",EDGE,"E82.sketch_text.stroke-25"),sQuery(id+"F4.wireOp",EDGE,"E82.sketch_text.stroke-26"),sQuery(id+"F4.wireOp",EDGE,"E82.sketch_text.stroke-31"),sQuery(id+"F4.wireOp",EDGE,"E82.sketch_text.stroke-32"),sQuery(id+"F4.wireOp",EDGE,"E82.sketch_text.stroke-33"),sQuery(id+"F4.wireOp",EDGE,"E82.sketch_text.stroke-34"),sQuery(id+"F4.wireOp",EDGE,"E82.sketch_text.stroke-35"),sQuery(id+"F4.wireOp",EDGE,"E82.sketch_text.stroke-36"),sQuery(id+"F4.wireOp",EDGE,"E82.sketch_text.stroke-37"),sQuery(id+"F4.wireOp",EDGE,"E82.sketch_text.stroke-38"),sQuery(id+"F4.wireOp",EDGE,"E82.sketch_text.stroke-39"),sQuery(id+"F4.wireOp",EDGE,"E82.sketch_text.stroke-40"),sQuery(id+"F4.wireOp",EDGE,"E82.sketch_text.stroke-41"),sQuery(id+"F4.wireOp",EDGE,"E82.sketch_text.stroke-42"),sQuery(id+"F4.wireOp",EDGE,"E82.sketch_text.stroke-43"),sQuery(id+"F4.wireOp",EDGE,"E82.sketch_text.stroke-44"),sQuery(id+"F4.wireOp",EDGE,"E82.sketch_text.stroke-49"),sQuery(id+"F4.wireOp",EDGE,"E82.sketch_text.stroke-50"),sQuery(id+"F4.wireOp",EDGE,"E82.sketch_text.stroke-51"),sQuery(id+"F4.wireOp",EDGE,"E82.sketch_text.stroke-52"),sQuery(id+"F4.wireOp",EDGE,"E82.sketch_text.stroke-53"),sQuery(id+"F4.wireOp",EDGE,"E82.sketch_text.stroke-54"),sQuery(id+"F4.wireOp",EDGE,"E82.sketch_text.stroke-55"),sQuery(id+"F4.wireOp",EDGE,"E82.sketch_text.stroke-56"),sQuery(id+"F4.wireOp",EDGE,"E82.sketch_text.stroke-57"),sQuery(id+"F4.wireOp",EDGE,"E82.sketch_text.stroke-58"),sQuery(id+"F4.wireOp",EDGE,"E82.sketch_text.stroke-59"),sQuery(id+"F4.wireOp",EDGE,"E82.sketch_text.stroke-60"),sQuery(id+"F4.wireOp",EDGE,"E82.sketch_text.stroke-61"),sQuery(id+"F4.wireOp",EDGE,"E82.sketch_text.stroke-62"),sQuery(id+"F4.wireOp",EDGE,"E82.sketch_text.stroke-63"),sQuery(id+"F4.wireOp",EDGE,"E82.sketch_text.stroke-64"),sQuery(id+"F4.wireOp",EDGE,"E82.sketch_text.stroke-65"),sQuery(id+"F4.wireOp",EDGE,"E82.sketch_text.stroke-66"),sQuery(id+"F4.wireOp",EDGE,"E82.sketch_text.stroke-67"),sQuery(id+"F4.wireOp",EDGE,"E82.sketch_text.stroke-68"),sQuery(id+"F4.wireOp",EDGE,"E82.sketch_text.stroke-69"),sQuery(id+"F4.wireOp",EDGE,"E82.sketch_text.stroke-70"),sQuery(id+"F4.wireOp",EDGE,"E82.sketch_text.stroke-71"),sQuery(id+"F4.wireOp",EDGE,"E82.sketch_text.stroke-72"),sQuery(id+"F4.wireOp",EDGE,"E82.sketch_text.stroke-73"),sQuery(id+"F4.wireOp",EDGE,"E82.sketch_text.stroke-74"),sQuery(id+"F4.wireOp",EDGE,"E82.sketch_text.stroke-75"),sQuery(id+"F4.wireOp",EDGE,"E82.sketch_text.stroke-76"),sQuery(id+"F4.wireOp",EDGE,"E82.sketch_text.stroke-77"),sQuery(id+"F4.wireOp",EDGE,"E82.sketch_text.stroke-78"),sQuery(id+"F4.wireOp",EDGE,"E82.sketch_text.stroke-79"),sQuery(id+"F4.wireOp",EDGE,"E82.sketch_text.stroke-80"),sQuery(id+"F4.wireOp",EDGE,"E82.sketch_text.stroke-81"),sQuery(id+"F4.wireOp",EDGE,"E82.sketch_text.stroke-82"),sQuery(id+"F4.wireOp",EDGE,"E82.sketch_text.stroke-83"),sQuery(id+"F4.wireOp",EDGE,"E82.sketch_text.stroke-84"),sQuery(id+"F4.wireOp",EDGE,"E82.sketch_text.stroke-85"),sQuery(id+"F4.wireOp",EDGE,"E82.sketch_text.stroke-86"),sQuery(id+"F4.wireOp",EDGE,"E82.sketch_text.stroke-87"),sQuery(id+"F4.wireOp",EDGE,"E82.sketch_text.stroke-88"),sQuery(id+"F4.wireOp",EDGE,"E82.sketch_text.stroke-89"),sQuery(id+"F4.wireOp",EDGE,"E82.sketch_text.stroke-90"),sQuery(id+"F4.wireOp",EDGE,"E82.sketch_text.stroke-91"),sQuery(id+"F4.wireOp",EDGE,"E82.sketch_text.stroke-92"),sQuery(id+"F4.wireOp",EDGE,"E82.sketch_text.stroke-93"),sQuery(id+"F4.wireOp",EDGE,"E82.sketch_text.stroke-94"),sQuery(id+"F4.wireOp",EDGE,"E82.sketch_text.stroke-95"),sQuery(id+"F4.wireOp",EDGE,"E82.sketch_text.stroke-96"),sQuery(id+"F4.wireOp",EDGE,"E82.sketch_text.stroke-97"),sQuery(id+"F4.wireOp",EDGE,"E82.sketch_text.stroke-98")])],"isStart":true})]});
            var sketch = newSketch(context, id + "F6", { "sketchPlane" : qUnion([Q0])});
            skLineSegment(sketch, "E83.bottom", {"start": v(-17.3, -18.36) * mm, "end": v(-16.1, -18.36) * mm});
            skLineSegment(sketch, "E83.top", {"start": v(-17.3, -10.82) * mm, "end": v(-16.1, -10.82) * mm});
            skLineSegment(sketch, "E83.left", {"start": v(-17.3, -18.36) * mm, "end": v(-17.3, -10.82) * mm});
            skLineSegment(sketch, "E83.right", {"start": v(-16.1, -18.36) * mm, "end": v(-16.1, -10.82) * mm});
            skLineSegment(sketch, "E84.bottom", {"start": v(-0.01, -18.36) * mm, "end": v(1.19, -18.36) * mm});
            skLineSegment(sketch, "E84.top", {"start": v(-0.01, -10.82) * mm, "end": v(1.19, -10.82) * mm});
            skLineSegment(sketch, "E84.left", {"start": v(-0.01, -18.36) * mm, "end": v(-0.01, -10.82) * mm});
            skLineSegment(sketch, "E84.right", {"start": v(1.19, -18.36) * mm, "end": v(1.19, -10.82) * mm});
            skLineSegment(sketch, "E85.bottom", {"start": v(39.6, -18.36) * mm, "end": v(40.8, -18.36) * mm});
            skLineSegment(sketch, "E85.top", {"start": v(39.6, -10.82) * mm, "end": v(40.8, -10.82) * mm});
            skLineSegment(sketch, "E85.left", {"start": v(39.6, -18.36) * mm, "end": v(39.6, -10.82) * mm});
            skLineSegment(sketch, "E85.right", {"start": v(40.8, -18.36) * mm, "end": v(40.8, -10.82) * mm});
            skSolve(sketch);
        }
        {
            var Q0;
            Q0 = qSketchRegion(id + "F6", true);
            var Q1;
            {var subQ0=sQuery(id+"F0.wireOp",EDGE,"E70.MirrorCS");var subQ1=sQuery(id+"F0.wireOp",EDGE,"E69.MirrorCS");var subQ2=sQuery(id+"F0.wireOp",EDGE,"E68.MirrorCS");var subQ3=sQuery(id+"F0.wireOp",EDGE,"E67.MirrorCS");var subQ4=sQuery(id+"F0.wireOp",EDGE,"E66.MirrorCS");var subQ5=sQuery(id+"F0.wireOp",EDGE,"E65.MirrorCS");var subQ6=sQuery(id+"F0.wireOp",EDGE,"E64.MirrorCS");var subQ7=sQuery(id+"F0.wireOp",EDGE,"E61.MirrorCS");var subQ8=sQuery(id+"F0.wireOp",EDGE,"E60.MirrorCS");var subQ9=sQuery(id+"F0.wireOp",EDGE,"E59.MirrorCS");var subQ10=sQuery(id+"F0.wireOp",EDGE,"E58.MirrorCS");var subQ11=sQuery(id+"F0.wireOp",EDGE,"E57.MirrorCS");var subQ12=sQuery(id+"F0.wireOp",EDGE,"E55.MirrorCS");var subQ13=sQuery(id+"F0.wireOp",EDGE,"E54.MirrorCS");var subQ14=sQuery(id+"F0.wireOp",EDGE,"E53.MirrorCS");var subQ15=sQuery(id+"F0.wireOp",EDGE,"E52.MirrorCS");var subQ16=sQuery(id+"F0.wireOp",EDGE,"E51.MirrorCS");var subQ17=sQuery(id+"F0.wireOp",EDGE,"E50.MirrorCS");var subQ18=sQuery(id+"F0.wireOp",EDGE,"E49.MirrorCS");var subQ19=sQuery(id+"F0.wireOp",EDGE,"E48.MirrorCS");var subQ20=sQuery(id+"F0.wireOp",EDGE,"E47.MirrorCS");var subQ21=sQuery(id+"F0.wireOp",EDGE,"E46.MirrorCS");var subQ22=sQuery(id+"F0.wireOp",EDGE,"E45.MirrorCS");var subQ23=sQuery(id+"F0.wireOp",EDGE,"E44.MirrorCS");var subQ24=sQuery(id+"F0.wireOp",EDGE,"E43.MirrorCS");var subQ25=sQuery(id+"F0.wireOp",EDGE,"E42.MirrorCS");var subQ26=sQuery(id+"F0.wireOp",EDGE,"E41.MirrorCS");var subQ27=sQuery(id+"F0.wireOp",EDGE,"E40.MirrorCS");var subQ28=sQuery(id+"F0.wireOp",EDGE,"E39.MirrorCS");var subQ29=sQuery(id+"F0.wireOp",EDGE,"E38.MirrorCS");var subQ30=sQuery(id+"F0.wireOp",EDGE,"E37.MirrorCS");var subQ31=sQuery(id+"F0.wireOp",EDGE,"E36.MirrorCS");var subQ32=sQuery(id+"F0.wireOp",EDGE,"E35");var subQ33=sQuery(id+"F0.wireOp",EDGE,"E33");var subQ34=sQuery(id+"F0.wireOp",EDGE,"E32");var subQ35=sQuery(id+"F0.wireOp",EDGE,"E31");var subQ36=sQuery(id+"F0.wireOp",EDGE,"E30");var subQ37=sQuery(id+"F0.wireOp",EDGE,"E29");var subQ38=sQuery(id+"F0.wireOp",EDGE,"E28");var subQ39=sQuery(id+"F0.wireOp",EDGE,"E27");var subQ40=sQuery(id+"F0.wireOp",EDGE,"E26");var subQ41=sQuery(id+"F0.wireOp",EDGE,"E25");var subQ42=sQuery(id+"F0.wireOp",EDGE,"E24");var subQ43=sQuery(id+"F0.wireOp",EDGE,"E23");var subQ44=sQuery(id+"F0.wireOp",EDGE,"E22");var subQ45=sQuery(id+"F0.wireOp",EDGE,"E21.MirrorCS");var subQ46=sQuery(id+"F0.wireOp",EDGE,"E20");var subQ47=sQuery(id+"F0.wireOp",EDGE,"E19");var subQ48=sQuery(id+"F0.wireOp",EDGE,"E18.MirrorCS");var subQ49=sQuery(id+"F0.wireOp",EDGE,"E17.MirrorCS");var subQ50=sQuery(id+"F0.wireOp",EDGE,"E16.MirrorCS");var subQ51=sQuery(id+"F0.wireOp",EDGE,"E15.MirrorCS");var subQ52=sQuery(id+"F0.wireOp",EDGE,"E14.MirrorCS");var subQ53=sQuery(id+"F0.wireOp",EDGE,"E12");var subQ54=sQuery(id+"F0.wireOp",EDGE,"E11");var subQ55=sQuery(id+"F0.wireOp",EDGE,"E10");var subQ56=sQuery(id+"F0.wireOp",EDGE,"E9");var subQ57=sQuery(id+"F0.wireOp",EDGE,"E8");var subQ58=sQuery(id+"F0.wireOp",EDGE,"E7");var subQ59=sQuery(id+"F0.wireOp",EDGE,"E6");var subQ60=sQuery(id+"F0.wireOp",EDGE,"E5");var subQ61=sQuery(id+"F0.wireOp",EDGE,"E4");var subQ62=sQuery(id+"F0.wireOp",EDGE,"E3");var subQ63=sQuery(id+"F0.wireOp",EDGE,"E2");Q1=makeQuery(id+"F5.boolean.opBoolean","MERGE",FACE,{"derivedFrom":[makeQuery(id+"F1.opExtrude","CAP_FACE",FACE,{"disambiguationData":[OSD([subQ63,subQ62,subQ61,subQ60,subQ59,subQ58,subQ57,subQ56,subQ55,subQ54,subQ53,subQ52,subQ51,subQ50,subQ49,subQ48,subQ47,subQ46,subQ45,subQ44,subQ43,subQ42,subQ41,subQ40,subQ39,subQ38,subQ37,subQ36,subQ35,subQ34,subQ33,subQ32,subQ31,subQ30,subQ29,subQ28,subQ27,subQ26,subQ25,subQ24,subQ23,subQ22,subQ21,subQ20,subQ19,subQ18,subQ17,subQ16,subQ15,subQ14,subQ13,subQ12,subQ11,subQ10,subQ9,subQ8,subQ7,subQ6,subQ5,subQ4,subQ3,subQ2,subQ1,subQ0])],"isStart":true}),makeQuery(id+"F5.opExtrude","CAP_FACE",FACE,{"disambiguationData":[OSD([subQ63,subQ62,subQ61,subQ60,subQ59,subQ58,subQ57,subQ56,subQ55,subQ54,subQ53,subQ52,subQ51,subQ50,subQ49,subQ48,subQ47,subQ46,subQ45,subQ44,subQ43,subQ42,subQ41,subQ40,subQ39,subQ38,subQ37,subQ36,subQ35,subQ34,subQ33,subQ32,subQ31,subQ30,subQ29,subQ28,subQ27,subQ26,subQ25,subQ24,subQ23,subQ22,subQ21,subQ20,subQ19,subQ18,subQ17,subQ16,subQ15,subQ14,subQ13,subQ12,subQ11,subQ10,subQ9,subQ8,subQ7,subQ6,subQ5,subQ4,subQ3,subQ2,subQ1,subQ0]),OD(0.0)],"isStart":false})]});}
            extrude(context, id + "F7", {"entities" : qUnion([Q0]), "operationType" : NewBodyOperationType.ADD, "endBound" : BoundingType.UP_TO_SURFACE, "oppositeDirection" : true, "depth" : 25 * mm, "endBoundEntityFace" : qUnion([Q1]), "offsetDistance" : 25 * mm});
        }
        {
            var Q0;
            Q0=makeQuery(id+"F7.boolean.opBoolean","MERGE",FACE,{"derivedFrom":[makeQuery(id+"F5.opExtrude","CAP_FACE",FACE,{"disambiguationData":[OSD([sQuery(id+"F4.wireOp",EDGE,"E82.sketch_text.stroke-27"),sQuery(id+"F4.wireOp",EDGE,"E82.sketch_text.stroke-28"),sQuery(id+"F4.wireOp",EDGE,"E82.sketch_text.stroke-29"),sQuery(id+"F4.wireOp",EDGE,"E82.sketch_text.stroke-30")])],"isStart":true}),makeQuery(id+"F5.opExtrude","CAP_FACE",FACE,{"disambiguationData":[OSD([sQuery(id+"F4.wireOp",EDGE,"E82.sketch_text.stroke-45"),sQuery(id+"F4.wireOp",EDGE,"E82.sketch_text.stroke-46"),sQuery(id+"F4.wireOp",EDGE,"E82.sketch_text.stroke-47"),sQuery(id+"F4.wireOp",EDGE,"E82.sketch_text.stroke-48")])],"isStart":true}),makeQuery(id+"F5.opExtrude","CAP_FACE",FACE,{"disambiguationData":[OSD([sQuery(id+"F4.wireOp",EDGE,"E82.sketch_text.stroke-99"),sQuery(id+"F4.wireOp",EDGE,"E82.sketch_text.stroke-100"),sQuery(id+"F4.wireOp",EDGE,"E82.sketch_text.stroke-101"),sQuery(id+"F4.wireOp",EDGE,"E82.sketch_text.stroke-102")])],"isStart":true}),makeQuery(id+"F5.boolean.opBoolean","MERGE",FACE,{"derivedFrom":[makeQuery(id+"F1.opExtrude","CAP_FACE",FACE,{"disambiguationData":[OSD([sQuery(id+"F0.wireOp",EDGE,"E2"),sQuery(id+"F0.wireOp",EDGE,"E3"),sQuery(id+"F0.wireOp",EDGE,"E4"),sQuery(id+"F0.wireOp",EDGE,"E5"),sQuery(id+"F0.wireOp",EDGE,"E6"),sQuery(id+"F0.wireOp",EDGE,"E7"),sQuery(id+"F0.wireOp",EDGE,"E8"),sQuery(id+"F0.wireOp",EDGE,"E9"),sQuery(id+"F0.wireOp",EDGE,"E10"),sQuery(id+"F0.wireOp",EDGE,"E11"),sQuery(id+"F0.wireOp",EDGE,"E12"),sQuery(id+"F0.wireOp",EDGE,"E14.MirrorCS"),sQuery(id+"F0.wireOp",EDGE,"E15.MirrorCS"),sQuery(id+"F0.wireOp",EDGE,"E16.MirrorCS"),sQuery(id+"F0.wireOp",EDGE,"E17.MirrorCS"),sQuery(id+"F0.wireOp",EDGE,"E18.MirrorCS"),sQuery(id+"F0.wireOp",EDGE,"E19"),sQuery(id+"F0.wireOp",EDGE,"E20"),sQuery(id+"F0.wireOp",EDGE,"E21.MirrorCS"),sQuery(id+"F0.wireOp",EDGE,"E22"),sQuery(id+"F0.wireOp",EDGE,"E23"),sQuery(id+"F0.wireOp",EDGE,"E24"),sQuery(id+"F0.wireOp",EDGE,"E25"),sQuery(id+"F0.wireOp",EDGE,"E26"),sQuery(id+"F0.wireOp",EDGE,"E27"),sQuery(id+"F0.wireOp",EDGE,"E28"),sQuery(id+"F0.wireOp",EDGE,"E29"),sQuery(id+"F0.wireOp",EDGE,"E30"),sQuery(id+"F0.wireOp",EDGE,"E31"),sQuery(id+"F0.wireOp",EDGE,"E32"),sQuery(id+"F0.wireOp",EDGE,"E33"),sQuery(id+"F0.wireOp",EDGE,"E35"),sQuery(id+"F0.wireOp",EDGE,"E36.MirrorCS"),sQuery(id+"F0.wireOp",EDGE,"E37.MirrorCS"),sQuery(id+"F0.wireOp",EDGE,"E38.MirrorCS"),sQuery(id+"F0.wireOp",EDGE,"E39.MirrorCS"),sQuery(id+"F0.wireOp",EDGE,"E40.MirrorCS"),sQuery(id+"F0.wireOp",EDGE,"E41.MirrorCS"),sQuery(id+"F0.wireOp",EDGE,"E42.MirrorCS"),sQuery(id+"F0.wireOp",EDGE,"E43.MirrorCS"),sQuery(id+"F0.wireOp",EDGE,"E44.MirrorCS"),sQuery(id+"F0.wireOp",EDGE,"E45.MirrorCS"),sQuery(id+"F0.wireOp",EDGE,"E46.MirrorCS"),sQuery(id+"F0.wireOp",EDGE,"E47.MirrorCS"),sQuery(id+"F0.wireOp",EDGE,"E48.MirrorCS"),sQuery(id+"F0.wireOp",EDGE,"E49.MirrorCS"),sQuery(id+"F0.wireOp",EDGE,"E50.MirrorCS"),sQuery(id+"F0.wireOp",EDGE,"E51.MirrorCS"),sQuery(id+"F0.wireOp",EDGE,"E52.MirrorCS"),sQuery(id+"F0.wireOp",EDGE,"E53.MirrorCS"),sQuery(id+"F0.wireOp",EDGE,"E54.MirrorCS"),sQuery(id+"F0.wireOp",EDGE,"E55.MirrorCS"),sQuery(id+"F0.wireOp",EDGE,"E57.MirrorCS"),sQuery(id+"F0.wireOp",EDGE,"E58.MirrorCS"),sQuery(id+"F0.wireOp",EDGE,"E59.MirrorCS"),sQuery(id+"F0.wireOp",EDGE,"E60.MirrorCS"),sQuery(id+"F0.wireOp",EDGE,"E61.MirrorCS"),sQuery(id+"F0.wireOp",EDGE,"E64.MirrorCS"),sQuery(id+"F0.wireOp",EDGE,"E65.MirrorCS"),sQuery(id+"F0.wireOp",EDGE,"E66.MirrorCS"),sQuery(id+"F0.wireOp",EDGE,"E67.MirrorCS"),sQuery(id+"F0.wireOp",EDGE,"E68.MirrorCS"),sQuery(id+"F0.wireOp",EDGE,"E69.MirrorCS"),sQuery(id+"F0.wireOp",EDGE,"E70.MirrorCS")])],"isStart":false}),makeQuery(id+"F5.opExtrude","CAP_FACE",FACE,{"disambiguationData":[OSD([sQuery(id+"F4.wireOp",EDGE,"E71"),sQuery(id+"F4.wireOp",EDGE,"E72"),sQuery(id+"F4.wireOp",EDGE,"E73"),sQuery(id+"F4.wireOp",EDGE,"E74"),sQuery(id+"F4.wireOp",EDGE,"E75"),sQuery(id+"F4.wireOp",EDGE,"E76"),sQuery(id+"F4.wireOp",EDGE,"E77"),sQuery(id+"F4.wireOp",EDGE,"E78"),sQuery(id+"F4.wireOp",EDGE,"E79"),sQuery(id+"F4.wireOp",EDGE,"E80"),sQuery(id+"F4.wireOp",EDGE,"E82.sketch_text.stroke-0"),sQuery(id+"F4.wireOp",EDGE,"E82.sketch_text.stroke-1"),sQuery(id+"F4.wireOp",EDGE,"E82.sketch_text.stroke-2"),sQuery(id+"F4.wireOp",EDGE,"E82.sketch_text.stroke-3"),sQuery(id+"F4.wireOp",EDGE,"E82.sketch_text.stroke-4"),sQuery(id+"F4.wireOp",EDGE,"E82.sketch_text.stroke-5"),sQuery(id+"F4.wireOp",EDGE,"E82.sketch_text.stroke-6"),sQuery(id+"F4.wireOp",EDGE,"E82.sketch_text.stroke-7"),sQuery(id+"F4.wireOp",EDGE,"E82.sketch_text.stroke-8"),sQuery(id+"F4.wireOp",EDGE,"E82.sketch_text.stroke-9"),sQuery(id+"F4.wireOp",EDGE,"E82.sketch_text.stroke-10"),sQuery(id+"F4.wireOp",EDGE,"E82.sketch_text.stroke-11"),sQuery(id+"F4.wireOp",EDGE,"E82.sketch_text.stroke-12"),sQuery(id+"F4.wireOp",EDGE,"E82.sketch_text.stroke-13"),sQuery(id+"F4.wireOp",EDGE,"E82.sketch_text.stroke-14"),sQuery(id+"F4.wireOp",EDGE,"E82.sketch_text.stroke-15"),sQuery(id+"F4.wireOp",EDGE,"E82.sketch_text.stroke-16"),sQuery(id+"F4.wireOp",EDGE,"E82.sketch_text.stroke-17"),sQuery(id+"F4.wireOp",EDGE,"E82.sketch_text.stroke-18"),sQuery(id+"F4.wireOp",EDGE,"E82.sketch_text.stroke-19"),sQuery(id+"F4.wireOp",EDGE,"E82.sketch_text.stroke-20"),sQuery(id+"F4.wireOp",EDGE,"E82.sketch_text.stroke-21"),sQuery(id+"F4.wireOp",EDGE,"E82.sketch_text.stroke-22"),sQuery(id+"F4.wireOp",EDGE,"E82.sketch_text.stroke-23"),sQuery(id+"F4.wireOp",EDGE,"E82.sketch_text.stroke-24"),sQuery(id+"F4.wireOp",EDGE,"E82.sketch_text.stroke-25"),sQuery(id+"F4.wireOp",EDGE,"E82.sketch_text.stroke-26"),sQuery(id+"F4.wireOp",EDGE,"E82.sketch_text.stroke-31"),sQuery(id+"F4.wireOp",EDGE,"E82.sketch_text.stroke-32"),sQuery(id+"F4.wireOp",EDGE,"E82.sketch_text.stroke-33"),sQuery(id+"F4.wireOp",EDGE,"E82.sketch_text.stroke-34"),sQuery(id+"F4.wireOp",EDGE,"E82.sketch_text.stroke-35"),sQuery(id+"F4.wireOp",EDGE,"E82.sketch_text.stroke-36"),sQuery(id+"F4.wireOp",EDGE,"E82.sketch_text.stroke-37"),sQuery(id+"F4.wireOp",EDGE,"E82.sketch_text.stroke-38"),sQuery(id+"F4.wireOp",EDGE,"E82.sketch_text.stroke-39"),sQuery(id+"F4.wireOp",EDGE,"E82.sketch_text.stroke-40"),sQuery(id+"F4.wireOp",EDGE,"E82.sketch_text.stroke-41"),sQuery(id+"F4.wireOp",EDGE,"E82.sketch_text.stroke-42"),sQuery(id+"F4.wireOp",EDGE,"E82.sketch_text.stroke-43"),sQuery(id+"F4.wireOp",EDGE,"E82.sketch_text.stroke-44"),sQuery(id+"F4.wireOp",EDGE,"E82.sketch_text.stroke-49"),sQuery(id+"F4.wireOp",EDGE,"E82.sketch_text.stroke-50"),sQuery(id+"F4.wireOp",EDGE,"E82.sketch_text.stroke-51"),sQuery(id+"F4.wireOp",EDGE,"E82.sketch_text.stroke-52"),sQuery(id+"F4.wireOp",EDGE,"E82.sketch_text.stroke-53"),sQuery(id+"F4.wireOp",EDGE,"E82.sketch_text.stroke-54"),sQuery(id+"F4.wireOp",EDGE,"E82.sketch_text.stroke-55"),sQuery(id+"F4.wireOp",EDGE,"E82.sketch_text.stroke-56"),sQuery(id+"F4.wireOp",EDGE,"E82.sketch_text.stroke-57"),sQuery(id+"F4.wireOp",EDGE,"E82.sketch_text.stroke-58"),sQuery(id+"F4.wireOp",EDGE,"E82.sketch_text.stroke-59"),sQuery(id+"F4.wireOp",EDGE,"E82.sketch_text.stroke-60"),sQuery(id+"F4.wireOp",EDGE,"E82.sketch_text.stroke-61"),sQuery(id+"F4.wireOp",EDGE,"E82.sketch_text.stroke-62"),sQuery(id+"F4.wireOp",EDGE,"E82.sketch_text.stroke-63"),sQuery(id+"F4.wireOp",EDGE,"E82.sketch_text.stroke-64"),sQuery(id+"F4.wireOp",EDGE,"E82.sketch_text.stroke-65"),sQuery(id+"F4.wireOp",EDGE,"E82.sketch_text.stroke-66"),sQuery(id+"F4.wireOp",EDGE,"E82.sketch_text.stroke-67"),sQuery(id+"F4.wireOp",EDGE,"E82.sketch_text.stroke-68"),sQuery(id+"F4.wireOp",EDGE,"E82.sketch_text.stroke-69"),sQuery(id+"F4.wireOp",EDGE,"E82.sketch_text.stroke-70"),sQuery(id+"F4.wireOp",EDGE,"E82.sketch_text.stroke-71"),sQuery(id+"F4.wireOp",EDGE,"E82.sketch_text.stroke-72"),sQuery(id+"F4.wireOp",EDGE,"E82.sketch_text.stroke-73"),sQuery(id+"F4.wireOp",EDGE,"E82.sketch_text.stroke-74"),sQuery(id+"F4.wireOp",EDGE,"E82.sketch_text.stroke-75"),sQuery(id+"F4.wireOp",EDGE,"E82.sketch_text.stroke-76"),sQuery(id+"F4.wireOp",EDGE,"E82.sketch_text.stroke-77"),sQuery(id+"F4.wireOp",EDGE,"E82.sketch_text.stroke-78"),sQuery(id+"F4.wireOp",EDGE,"E82.sketch_text.stroke-79"),sQuery(id+"F4.wireOp",EDGE,"E82.sketch_text.stroke-80"),sQuery(id+"F4.wireOp",EDGE,"E82.sketch_text.stroke-81"),sQuery(id+"F4.wireOp",EDGE,"E82.sketch_text.stroke-82"),sQuery(id+"F4.wireOp",EDGE,"E82.sketch_text.stroke-83"),sQuery(id+"F4.wireOp",EDGE,"E82.sketch_text.stroke-84"),sQuery(id+"F4.wireOp",EDGE,"E82.sketch_text.stroke-85"),sQuery(id+"F4.wireOp",EDGE,"E82.sketch_text.stroke-86"),sQuery(id+"F4.wireOp",EDGE,"E82.sketch_text.stroke-87"),sQuery(id+"F4.wireOp",EDGE,"E82.sketch_text.stroke-88"),sQuery(id+"F4.wireOp",EDGE,"E82.sketch_text.stroke-89"),sQuery(id+"F4.wireOp",EDGE,"E82.sketch_text.stroke-90"),sQuery(id+"F4.wireOp",EDGE,"E82.sketch_text.stroke-91"),sQuery(id+"F4.wireOp",EDGE,"E82.sketch_text.stroke-92"),sQuery(id+"F4.wireOp",EDGE,"E82.sketch_text.stroke-93"),sQuery(id+"F4.wireOp",EDGE,"E82.sketch_text.stroke-94"),sQuery(id+"F4.wireOp",EDGE,"E82.sketch_text.stroke-95"),sQuery(id+"F4.wireOp",EDGE,"E82.sketch_text.stroke-96"),sQuery(id+"F4.wireOp",EDGE,"E82.sketch_text.stroke-97"),sQuery(id+"F4.wireOp",EDGE,"E82.sketch_text.stroke-98")])],"isStart":true})]}),makeQuery(id+"F7.opExtrude","CAP_FACE",FACE,{"disambiguationData":[OSD([sQuery(id+"F6.wireOp",EDGE,"E83.bottom"),sQuery(id+"F6.wireOp",EDGE,"E83.top"),sQuery(id+"F6.wireOp",EDGE,"E83.left"),sQuery(id+"F6.wireOp",EDGE,"E83.right")])],"isStart":true}),makeQuery(id+"F7.opExtrude","CAP_FACE",FACE,{"disambiguationData":[OSD([sQuery(id+"F6.wireOp",EDGE,"E84.bottom"),sQuery(id+"F6.wireOp",EDGE,"E84.top"),sQuery(id+"F6.wireOp",EDGE,"E84.left"),sQuery(id+"F6.wireOp",EDGE,"E84.right")])],"isStart":true}),makeQuery(id+"F7.opExtrude","CAP_FACE",FACE,{"disambiguationData":[OSD([sQuery(id+"F6.wireOp",EDGE,"E85.bottom"),sQuery(id+"F6.wireOp",EDGE,"E85.top"),sQuery(id+"F6.wireOp",EDGE,"E85.left"),sQuery(id+"F6.wireOp",EDGE,"E85.right")])],"isStart":true})]});
            var sketch = newSketch(context, id + "F8", { "sketchPlane" : qUnion([Q0])});
            skLineSegment(sketch, "E86", {"start": v(-40.17, -24.7) * mm, "end": v(-19.96, -59.7) * mm});
            skLineSegment(sketch, "E87", {"start": v(-19.96, -59.7) * mm, "end": v(34.37, -59.7) * mm});
            skLineSegment(sketch, "E88", {"start": v(34.37, -59.7) * mm, "end": v(54.58, -24.7) * mm});
            skLineSegment(sketch, "E89", {"start": v(-28.62, -24.7) * mm, "end": v(-14.19, -49.7) * mm});
            skLineSegment(sketch, "E90", {"start": v(-14.19, -49.7) * mm, "end": v(28.6, -49.7) * mm});
            skLineSegment(sketch, "E91", {"start": v(28.6, -49.7) * mm, "end": v(43.03, -24.7) * mm});
            skLineSegment(sketch, "E92", {"start": v(7.2, -24.7) * mm, "end": v(7.2, -59.7) * mm, "construction": true});
            skSolve(sketch);
        }
        {
            var Q0;
            Q0 = qSketchRegion(id + "F8", true);
            var Q1;
            {var subQ4=sQuery(id+"F8.wireOp",EDGE,"E86");Q1=makeQuery(id+"F8.imprint","IMPRINT",FACE,{"disambiguationData":[TD([[makeQuery(id+"F8.imprint","IMPRINT",EDGE,{"derivedFrom":subQ4}),1.0]])]});}
            var Q2;
            {var subQ0=sQuery(id+"F0.wireOp",EDGE,"E70.MirrorCS");var subQ1=sQuery(id+"F0.wireOp",EDGE,"E69.MirrorCS");var subQ2=sQuery(id+"F0.wireOp",EDGE,"E68.MirrorCS");var subQ3=sQuery(id+"F0.wireOp",EDGE,"E67.MirrorCS");var subQ4=sQuery(id+"F0.wireOp",EDGE,"E66.MirrorCS");var subQ5=sQuery(id+"F0.wireOp",EDGE,"E65.MirrorCS");var subQ6=sQuery(id+"F0.wireOp",EDGE,"E64.MirrorCS");var subQ7=sQuery(id+"F0.wireOp",EDGE,"E61.MirrorCS");var subQ8=sQuery(id+"F0.wireOp",EDGE,"E60.MirrorCS");var subQ9=sQuery(id+"F0.wireOp",EDGE,"E59.MirrorCS");var subQ10=sQuery(id+"F0.wireOp",EDGE,"E58.MirrorCS");var subQ11=sQuery(id+"F0.wireOp",EDGE,"E57.MirrorCS");var subQ12=sQuery(id+"F0.wireOp",EDGE,"E55.MirrorCS");var subQ13=sQuery(id+"F0.wireOp",EDGE,"E54.MirrorCS");var subQ14=sQuery(id+"F0.wireOp",EDGE,"E53.MirrorCS");var subQ15=sQuery(id+"F0.wireOp",EDGE,"E52.MirrorCS");var subQ16=sQuery(id+"F0.wireOp",EDGE,"E51.MirrorCS");var subQ17=sQuery(id+"F0.wireOp",EDGE,"E50.MirrorCS");var subQ18=sQuery(id+"F0.wireOp",EDGE,"E49.MirrorCS");var subQ19=sQuery(id+"F0.wireOp",EDGE,"E48.MirrorCS");var subQ20=sQuery(id+"F0.wireOp",EDGE,"E47.MirrorCS");var subQ21=sQuery(id+"F0.wireOp",EDGE,"E46.MirrorCS");var subQ22=sQuery(id+"F0.wireOp",EDGE,"E45.MirrorCS");var subQ23=sQuery(id+"F0.wireOp",EDGE,"E44.MirrorCS");var subQ24=sQuery(id+"F0.wireOp",EDGE,"E43.MirrorCS");var subQ25=sQuery(id+"F0.wireOp",EDGE,"E42.MirrorCS");var subQ26=sQuery(id+"F0.wireOp",EDGE,"E41.MirrorCS");var subQ27=sQuery(id+"F0.wireOp",EDGE,"E40.MirrorCS");var subQ28=sQuery(id+"F0.wireOp",EDGE,"E39.MirrorCS");var subQ29=sQuery(id+"F0.wireOp",EDGE,"E38.MirrorCS");var subQ30=sQuery(id+"F0.wireOp",EDGE,"E37.MirrorCS");var subQ31=sQuery(id+"F0.wireOp",EDGE,"E36.MirrorCS");var subQ32=sQuery(id+"F0.wireOp",EDGE,"E35");var subQ33=sQuery(id+"F0.wireOp",EDGE,"E33");var subQ34=sQuery(id+"F0.wireOp",EDGE,"E32");var subQ35=sQuery(id+"F0.wireOp",EDGE,"E31");var subQ36=sQuery(id+"F0.wireOp",EDGE,"E30");var subQ37=sQuery(id+"F0.wireOp",EDGE,"E29");var subQ38=sQuery(id+"F0.wireOp",EDGE,"E28");var subQ39=sQuery(id+"F0.wireOp",EDGE,"E27");var subQ40=sQuery(id+"F0.wireOp",EDGE,"E26");var subQ41=sQuery(id+"F0.wireOp",EDGE,"E25");var subQ42=sQuery(id+"F0.wireOp",EDGE,"E24");var subQ43=sQuery(id+"F0.wireOp",EDGE,"E23");var subQ44=sQuery(id+"F0.wireOp",EDGE,"E22");var subQ45=sQuery(id+"F0.wireOp",EDGE,"E21.MirrorCS");var subQ46=sQuery(id+"F0.wireOp",EDGE,"E20");var subQ47=sQuery(id+"F0.wireOp",EDGE,"E19");var subQ48=sQuery(id+"F0.wireOp",EDGE,"E18.MirrorCS");var subQ49=sQuery(id+"F0.wireOp",EDGE,"E17.MirrorCS");var subQ50=sQuery(id+"F0.wireOp",EDGE,"E16.MirrorCS");var subQ51=sQuery(id+"F0.wireOp",EDGE,"E15.MirrorCS");var subQ52=sQuery(id+"F0.wireOp",EDGE,"E14.MirrorCS");var subQ53=sQuery(id+"F0.wireOp",EDGE,"E12");var subQ54=sQuery(id+"F0.wireOp",EDGE,"E11");var subQ55=sQuery(id+"F0.wireOp",EDGE,"E10");var subQ56=sQuery(id+"F0.wireOp",EDGE,"E9");var subQ57=sQuery(id+"F0.wireOp",EDGE,"E8");var subQ58=sQuery(id+"F0.wireOp",EDGE,"E7");var subQ59=sQuery(id+"F0.wireOp",EDGE,"E6");var subQ60=sQuery(id+"F0.wireOp",EDGE,"E5");var subQ61=sQuery(id+"F0.wireOp",EDGE,"E4");var subQ62=sQuery(id+"F0.wireOp",EDGE,"E3");var subQ63=sQuery(id+"F0.wireOp",EDGE,"E2");Q2=makeQuery(id+"F7.boolean.opBoolean","MERGE",FACE,{"derivedFrom":[makeQuery(id+"F5.opExtrude","CAP_FACE",FACE,{"disambiguationData":[OSD([subQ63,subQ62,subQ61,subQ60,subQ59,subQ58,subQ57,subQ56,subQ55,subQ54,subQ53,subQ52,subQ51,subQ50,subQ49,subQ48,subQ47,subQ46,subQ45,subQ44,subQ43,subQ42,subQ41,subQ40,subQ39,subQ38,subQ37,subQ36,subQ35,subQ34,subQ33,subQ32,subQ31,subQ30,subQ29,subQ28,subQ27,subQ26,subQ25,subQ24,subQ23,subQ22,subQ21,subQ20,subQ19,subQ18,subQ17,subQ16,subQ15,subQ14,subQ13,subQ12,subQ11,subQ10,subQ9,subQ8,subQ7,subQ6,subQ5,subQ4,subQ3,subQ2,subQ1,subQ0]),OD(1.0)],"isStart":false}),makeQuery(id+"F5.opExtrude","CAP_FACE",FACE,{"disambiguationData":[OSD([subQ63,subQ62,subQ61,subQ60,subQ59,subQ58,subQ57,subQ56,subQ55,subQ54,subQ53,subQ52,subQ51,subQ50,subQ49,subQ48,subQ47,subQ46,subQ45,subQ44,subQ43,subQ42,subQ41,subQ40,subQ39,subQ38,subQ37,subQ36,subQ35,subQ34,subQ33,subQ32,subQ31,subQ30,subQ29,subQ28,subQ27,subQ26,subQ25,subQ24,subQ23,subQ22,subQ21,subQ20,subQ19,subQ18,subQ17,subQ16,subQ15,subQ14,subQ13,subQ12,subQ11,subQ10,subQ9,subQ8,subQ7,subQ6,subQ5,subQ4,subQ3,subQ2,subQ1,subQ0]),OD(2.0)],"isStart":false}),makeQuery(id+"F5.opExtrude","CAP_FACE",FACE,{"disambiguationData":[OSD([subQ63,subQ62,subQ61,subQ60,subQ59,subQ58,subQ57,subQ56,subQ55,subQ54,subQ53,subQ52,subQ51,subQ50,subQ49,subQ48,subQ47,subQ46,subQ45,subQ44,subQ43,subQ42,subQ41,subQ40,subQ39,subQ38,subQ37,subQ36,subQ35,subQ34,subQ33,subQ32,subQ31,subQ30,subQ29,subQ28,subQ27,subQ26,subQ25,subQ24,subQ23,subQ22,subQ21,subQ20,subQ19,subQ18,subQ17,subQ16,subQ15,subQ14,subQ13,subQ12,subQ11,subQ10,subQ9,subQ8,subQ7,subQ6,subQ5,subQ4,subQ3,subQ2,subQ1,subQ0]),OD(3.0)],"isStart":false}),makeQuery(id+"F5.boolean.opBoolean","MERGE",FACE,{"derivedFrom":[makeQuery(id+"F1.opExtrude","CAP_FACE",FACE,{"disambiguationData":[OSD([subQ63,subQ62,subQ61,subQ60,subQ59,subQ58,subQ57,subQ56,subQ55,subQ54,subQ53,subQ52,subQ51,subQ50,subQ49,subQ48,subQ47,subQ46,subQ45,subQ44,subQ43,subQ42,subQ41,subQ40,subQ39,subQ38,subQ37,subQ36,subQ35,subQ34,subQ33,subQ32,subQ31,subQ30,subQ29,subQ28,subQ27,subQ26,subQ25,subQ24,subQ23,subQ22,subQ21,subQ20,subQ19,subQ18,subQ17,subQ16,subQ15,subQ14,subQ13,subQ12,subQ11,subQ10,subQ9,subQ8,subQ7,subQ6,subQ5,subQ4,subQ3,subQ2,subQ1,subQ0])],"isStart":true}),makeQuery(id+"F5.opExtrude","CAP_FACE",FACE,{"disambiguationData":[OSD([subQ63,subQ62,subQ61,subQ60,subQ59,subQ58,subQ57,subQ56,subQ55,subQ54,subQ53,subQ52,subQ51,subQ50,subQ49,subQ48,subQ47,subQ46,subQ45,subQ44,subQ43,subQ42,subQ41,subQ40,subQ39,subQ38,subQ37,subQ36,subQ35,subQ34,subQ33,subQ32,subQ31,subQ30,subQ29,subQ28,subQ27,subQ26,subQ25,subQ24,subQ23,subQ22,subQ21,subQ20,subQ19,subQ18,subQ17,subQ16,subQ15,subQ14,subQ13,subQ12,subQ11,subQ10,subQ9,subQ8,subQ7,subQ6,subQ5,subQ4,subQ3,subQ2,subQ1,subQ0]),OD(0.0)],"isStart":false})]}),makeQuery(id+"F7.opExtrude","CAP_FACE",FACE,{"disambiguationData":[OSD([subQ63,subQ62,subQ61,subQ60,subQ59,subQ58,subQ57,subQ56,subQ55,subQ54,subQ53,subQ52,subQ51,subQ50,subQ49,subQ48,subQ47,subQ46,subQ45,subQ44,subQ43,subQ42,subQ41,subQ40,subQ39,subQ38,subQ37,subQ36,subQ35,subQ34,subQ33,subQ32,subQ31,subQ30,subQ29,subQ28,subQ27,subQ26,subQ25,subQ24,subQ23,subQ22,subQ21,subQ20,subQ19,subQ18,subQ17,subQ16,subQ15,subQ14,subQ13,subQ12,subQ11,subQ10,subQ9,subQ8,subQ7,subQ6,subQ5,subQ4,subQ3,subQ2,subQ1,subQ0]),OD(0.0)],"isStart":false}),makeQuery(id+"F7.opExtrude","CAP_FACE",FACE,{"disambiguationData":[OSD([subQ63,subQ62,subQ61,subQ60,subQ59,subQ58,subQ57,subQ56,subQ55,subQ54,subQ53,subQ52,subQ51,subQ50,subQ49,subQ48,subQ47,subQ46,subQ45,subQ44,subQ43,subQ42,subQ41,subQ40,subQ39,subQ38,subQ37,subQ36,subQ35,subQ34,subQ33,subQ32,subQ31,subQ30,subQ29,subQ28,subQ27,subQ26,subQ25,subQ24,subQ23,subQ22,subQ21,subQ20,subQ19,subQ18,subQ17,subQ16,subQ15,subQ14,subQ13,subQ12,subQ11,subQ10,subQ9,subQ8,subQ7,subQ6,subQ5,subQ4,subQ3,subQ2,subQ1,subQ0]),OD(1.0)],"isStart":false}),makeQuery(id+"F7.opExtrude","CAP_FACE",FACE,{"disambiguationData":[OSD([subQ63,subQ62,subQ61,subQ60,subQ59,subQ58,subQ57,subQ56,subQ55,subQ54,subQ53,subQ52,subQ51,subQ50,subQ49,subQ48,subQ47,subQ46,subQ45,subQ44,subQ43,subQ42,subQ41,subQ40,subQ39,subQ38,subQ37,subQ36,subQ35,subQ34,subQ33,subQ32,subQ31,subQ30,subQ29,subQ28,subQ27,subQ26,subQ25,subQ24,subQ23,subQ22,subQ21,subQ20,subQ19,subQ18,subQ17,subQ16,subQ15,subQ14,subQ13,subQ12,subQ11,subQ10,subQ9,subQ8,subQ7,subQ6,subQ5,subQ4,subQ3,subQ2,subQ1,subQ0]),OD(2.0)],"isStart":false})]});}
            extrude(context, id + "F9", {"entities" : qUnion([Q0, Q1]), "operationType" : NewBodyOperationType.ADD, "endBound" : BoundingType.UP_TO_SURFACE, "oppositeDirection" : true, "depth" : 25 * mm, "endBoundEntityFace" : qUnion([Q2]), "offsetDistance" : 25 * mm});
        }
        {
            var Q0;
            Q0=makeQuery(id+"F9.opExtrude","SWEPT_EDGE",EDGE,{"disambiguationData":[OSD([sQuery(id+"F8.wireOp",EDGE,"E89"),sQuery(id+"F8.wireOp",EDGE,"E90")])]});
            var Q1;
            Q1=makeQuery(id+"F9.opExtrude","SWEPT_EDGE",EDGE,{"disambiguationData":[OSD([sQuery(id+"F8.wireOp",EDGE,"E90"),sQuery(id+"F8.wireOp",EDGE,"E91")])]});
            fillet(context, id + "F10", {"entities" : qUnion([Q0, Q1]), "radius" : 5 * mm, "tangentPropagation" : true, "allowEdgeOverflow" : false});
        }
        {
            var Q0;
            Q0=makeQuery(id+"F9.opExtrude","SWEPT_EDGE",EDGE,{"disambiguationData":[OSD([sQuery(id+"F8.wireOp",EDGE,"E86"),sQuery(id+"F8.wireOp",EDGE,"E87")])]});
            var Q1;
            Q1=makeQuery(id+"F9.opExtrude","SWEPT_EDGE",EDGE,{"disambiguationData":[OSD([sQuery(id+"F8.wireOp",EDGE,"E87"),sQuery(id+"F8.wireOp",EDGE,"E88")])]});
            fillet(context, id + "F11", {"entities" : qUnion([Q0, Q1]), "radius" : 15 * mm, "tangentPropagation" : true, "allowEdgeOverflow" : false});
        }
        {
            var Q0;
            Q0=makeQuery(id+"F5.opExtrude","SWEPT_EDGE",EDGE,{"disambiguationData":[OSD([sQuery(id+"F4.wireOp",EDGE,"E74"),sQuery(id+"F4.wireOp",EDGE,"E75")])]});
            var Q1;
            Q1=makeQuery(id+"F5.opExtrude","SWEPT_EDGE",EDGE,{"disambiguationData":[OSD([sQuery(id+"F4.wireOp",EDGE,"E73"),sQuery(id+"F4.wireOp",EDGE,"E74")])]});
            var Q2;
            Q2=makeQuery(id+"F5.opExtrude","SWEPT_EDGE",EDGE,{"disambiguationData":[OSD([sQuery(id+"F4.wireOp",EDGE,"E78"),sQuery(id+"F4.wireOp",EDGE,"E79")])]});
            var Q3;
            Q3=makeQuery(id+"F5.opExtrude","SWEPT_EDGE",EDGE,{"disambiguationData":[OSD([sQuery(id+"F4.wireOp",EDGE,"E77"),sQuery(id+"F4.wireOp",EDGE,"E78")])]});
            var Q4;
            Q4=makeQuery(id+"F5.opExtrude","SWEPT_EDGE",EDGE,{"disambiguationData":[OSD([sQuery(id+"F4.wireOp",EDGE,"E75"),sQuery(id+"F4.wireOp",EDGE,"E76")])]});
            var Q5;
            Q5=makeQuery(id+"F5.opExtrude","SWEPT_EDGE",EDGE,{"disambiguationData":[OSD([sQuery(id+"F4.wireOp",EDGE,"E76"),sQuery(id+"F4.wireOp",EDGE,"E77")])]});
            fillet(context, id + "F12", {"entities" : qUnion([Q0, Q1, Q2, Q3, Q4, Q5]), "radius" : 5 * mm, "tangentPropagation" : true, "allowEdgeOverflow" : false});
        }
        {
            var Q0;
            Q0=qCreatedBy(makeId("Right.planeOp"),FACE);
            var sketch = newSketch(context, id + "F13", { "sketchPlane" : qUnion([Q0])});
            skLineSegment(sketch, "E93.bottom", {"start": v(-4, 57.12) * mm, "end": v(-1.6, 57.12) * mm});
            skLineSegment(sketch, "E93.top", {"start": v(-4, -61.7) * mm, "end": v(-1.6, -61.7) * mm});
            skLineSegment(sketch, "E93.left", {"start": v(-4, 57.12) * mm, "end": v(-4, -61.7) * mm});
            skLineSegment(sketch, "E93.right", {"start": v(-1.6, 57.12) * mm, "end": v(-1.6, -61.7) * mm});
            skSolve(sketch);
        }
        {
            var Q0;
            Q0 = qSketchRegion(id + "F13", true);
            extrude(context, id + "F14", {"entities" : qUnion([Q0]), "operationType" : NewBodyOperationType.REMOVE, "endBound" : BoundingType.THROUGH_ALL, "oppositeDirection" : true, "depth" : 25 * mm, "offsetDistance" : 25 * mm, "hasSecondDirection" : true, "secondDirectionBound" : SecondDirectionBoundingType.THROUGH_ALL, "secondDirectionOppositeDirection" : false, "secondDirectionDepth" : 25 * mm});
        }
    });
